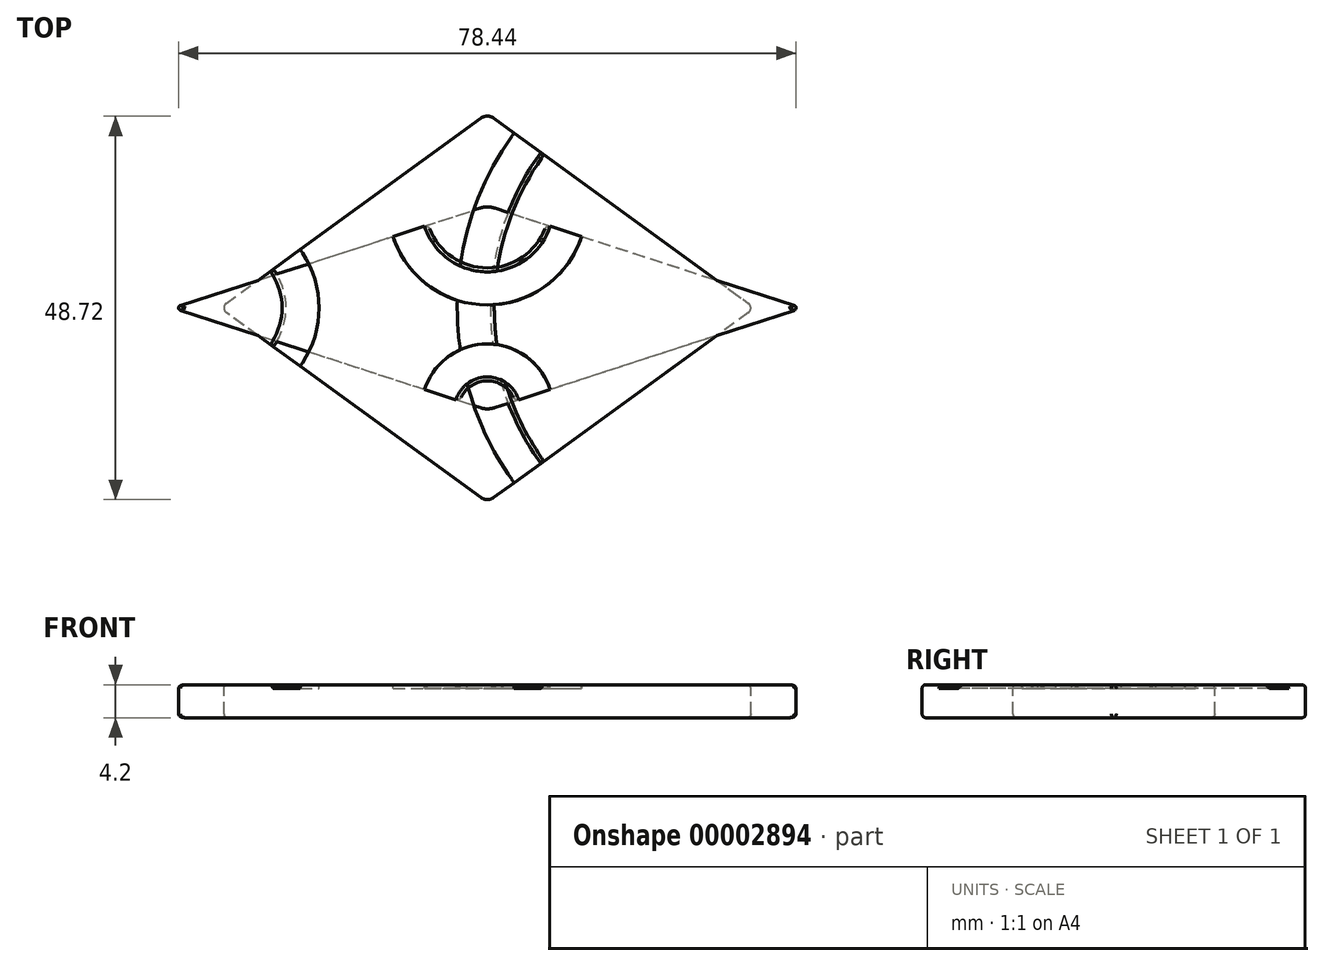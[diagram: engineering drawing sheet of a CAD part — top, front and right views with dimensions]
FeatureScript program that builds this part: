
annotation { "Feature Type Name" : "Feature", "Feature Type Description" : "" }
export const myFeature = defineFeature(function(context is Context, id is Id, definition is map)
    precondition{}
    {
        {
            var Q0;
            Q0=qCreatedBy(makeId("Top.planeOp"),FACE);
            var sketch = newSketch(context, id + "F0", { "sketchPlane" : qUnion([Q0])});
            skLineSegment(sketch, "E0", {"start": v(0.8, 24.1) * mm, "end": v(33.17, 0.59) * mm});
            skLineSegment(sketch, "E1", {"start": v(33.17, -0.59) * mm, "end": v(0.8, -24.1) * mm});
            skLineSegment(sketch, "E2", {"start": v(-0.8, -24.1) * mm, "end": v(-33.17, -0.59) * mm});
            skLineSegment(sketch, "E3", {"start": v(-33.17, 0.59) * mm, "end": v(-0.8, 24.1) * mm});
            skPoint(sketch, "E4.visualSharp", {"position": v(0, 24.69) * mm});
            skArc(sketch, "E4.filletArc", {"start": v(0.8, 24.1) * mm, "mid": v(0, 24.36) * mm, "end": v(-0.8, 24.1) * mm});
            skPoint(sketch, "E5.visualSharp", {"position": v(33.98, 0) * mm});
            skArc(sketch, "E5.filletArc", {"start": v(33.17, -0.59) * mm, "mid": v(33.47, 0) * mm, "end": v(33.17, 0.59) * mm});
            skPoint(sketch, "E6.visualSharp", {"position": v(0, -24.69) * mm});
            skArc(sketch, "E6.filletArc", {"start": v(-0.8, -24.1) * mm, "mid": v(0, -24.36) * mm, "end": v(0.8, -24.1) * mm});
            skPoint(sketch, "E7.visualSharp", {"position": v(-33.98, 0) * mm});
            skArc(sketch, "E7.filletArc", {"start": v(-33.17, 0.59) * mm, "mid": v(-33.47, 0) * mm, "end": v(-33.17, -0.59) * mm});
            skArc(sketch, "E8", {"start": v(6.8, 19.75) * mm, "mid": v(0.38, 0) * mm, "end": v(6.8, -19.75) * mm});
            skArc(sketch, "E9", {"start": v(3.4, 22.22) * mm, "mid": v(-3.82, 0) * mm, "end": v(3.4, -22.22) * mm});
            skArc(sketch, "E10", {"start": v(-27.18, -4.94) * mm, "mid": v(-25.58, 0) * mm, "end": v(-27.18, 4.94) * mm});
            skArc(sketch, "E11", {"start": v(-23.79, -7.4) * mm, "mid": v(-21.38, 0) * mm, "end": v(-23.79, 7.4) * mm});
            skSolve(sketch);
        }
        {
            var Q0;
            Q0 = qSketchRegion(id + "F0", true);
            extrude(context, id + "F1", {"entities" : qUnion([Q0]), "oppositeDirection" : true, "depth" : 4.2 * mm});
        }
        {
            var Q0;
            Q0=makeQuery(id+"F1.opExtrude","CAP_EDGE",EDGE,{"disambiguationData":[OSD([sQuery(id+"F0.wireOp",EDGE,"E2")])],"isStart":true});
            var Q1;
            Q1=makeQuery(id+"F1.opExtrude","CAP_EDGE",EDGE,{"disambiguationData":[OSD([sQuery(id+"F0.wireOp",EDGE,"E2")])],"isStart":false});
            fillet(context, id + "F2", {"entities" : qUnion([Q0, Q1]), "radius" : 0.5 * mm, "tangentPropagation" : true, "allowEdgeOverflow" : false});
        }
        {
            var Q0;
            {var subQ1=sQuery(id+"F0.wireOp",EDGE,"E8");Q0=makeQuery(id+"F0.imprint","IMPRINT",FACE,{"disambiguationData":[TD([[makeQuery(id+"F0.imprint","IMPRINT",EDGE,{"derivedFrom":subQ1}),-1.0]])]});}
            var Q1;
            {var subQ1=sQuery(id+"F0.wireOp",EDGE,"E10");Q1=makeQuery(id+"F0.imprint","IMPRINT",FACE,{"disambiguationData":[TD([[makeQuery(id+"F0.imprint","IMPRINT",EDGE,{"derivedFrom":subQ1}),-1.0]])]});}
            extrude(context, id + "F3", {"entities" : qUnion([Q0, Q1]), "operationType" : NewBodyOperationType.REMOVE, "oppositeDirection" : true, "depth" : 0.5 * mm});
        }
        {
            var Q0;
            Q0=makeQuery(id+"F3.boolean.opBoolean","COPY",EDGE,{"derivedFrom":makeQuery(id+"F3.opExtrude","CAP_EDGE",EDGE,{"disambiguationData":[OSD([sQuery(id+"F0.wireOp",EDGE,"E10")])],"isStart":true})});
            var Q1;
            Q1=makeQuery(id+"F3.boolean.opBoolean","COPY",EDGE,{"derivedFrom":makeQuery(id+"F3.opExtrude","CAP_EDGE",EDGE,{"disambiguationData":[OSD([sQuery(id+"F0.wireOp",EDGE,"E11")])],"isStart":true})});
            var Q2;
            Q2=makeQuery(id+"F3.boolean.opBoolean","COPY",EDGE,{"derivedFrom":makeQuery(id+"F3.opExtrude","CAP_EDGE",EDGE,{"disambiguationData":[OSD([sQuery(id+"F0.wireOp",EDGE,"E9")])],"isStart":true})});
            var Q3;
            Q3=makeQuery(id+"F3.boolean.opBoolean","COPY",EDGE,{"derivedFrom":makeQuery(id+"F3.opExtrude","CAP_EDGE",EDGE,{"disambiguationData":[OSD([sQuery(id+"F0.wireOp",EDGE,"E8")])],"isStart":true})});
            chamfer(context, id + "F4", {"entities" : qUnion([Q0, Q1, Q2, Q3]), "width" : 0.5 * mm, "tangentPropagation" : true});
        }
        {
            var Q0;
            Q0=qCreatedBy(makeId("Top.planeOp"),FACE);
            var sketch = newSketch(context, id + "F5", { "sketchPlane" : qUnion([Q0])});
            skLineSegment(sketch, "E12", {"start": v(-39, 0.3) * mm, "end": v(-0.95, 12.67) * mm});
            skLineSegment(sketch, "E13", {"start": v(0.95, 12.67) * mm, "end": v(39, 0.3) * mm});
            skLineSegment(sketch, "E14", {"start": v(39, -0.3) * mm, "end": v(0.95, -12.67) * mm});
            skLineSegment(sketch, "E15", {"start": v(-0.95, -12.67) * mm, "end": v(-39, -0.3) * mm});
            skPoint(sketch, "E16.visualSharp", {"position": v(0, 12.98) * mm});
            skArc(sketch, "E16.filletArc", {"start": v(0.95, 12.67) * mm, "mid": v(0, 12.82) * mm, "end": v(-0.95, 12.67) * mm});
            skPoint(sketch, "E17.visualSharp", {"position": v(39.94, 0) * mm});
            skArc(sketch, "E17.filletArc", {"start": v(39, -0.3) * mm, "mid": v(39.22, 0) * mm, "end": v(39, 0.3) * mm});
            skPoint(sketch, "E18.visualSharp", {"position": v(0, -12.98) * mm});
            skArc(sketch, "E18.filletArc", {"start": v(-0.95, -12.67) * mm, "mid": v(0, -12.82) * mm, "end": v(0.95, -12.67) * mm});
            skPoint(sketch, "E19.visualSharp", {"position": v(-39.94, 0) * mm});
            skArc(sketch, "E19.filletArc", {"start": v(-39, 0.3) * mm, "mid": v(-39.22, 0) * mm, "end": v(-39, -0.3) * mm});
            skArc(sketch, "E20", {"start": v(-7.99, 10.38) * mm, "mid": v(0, 4.58) * mm, "end": v(7.99, 10.38) * mm});
            skArc(sketch, "E21", {"start": v(-11.98, 9.09) * mm, "mid": v(0, 0.38) * mm, "end": v(11.98, 9.09) * mm});
            skArc(sketch, "E22", {"start": v(4, -11.68) * mm, "mid": v(0, -8.78) * mm, "end": v(-4, -11.68) * mm});
            skArc(sketch, "E23", {"start": v(7.99, -10.38) * mm, "mid": v(0, -4.58) * mm, "end": v(-7.99, -10.38) * mm});
            skSolve(sketch);
        }
        {
            var Q0;
            Q0 = qSketchRegion(id + "F5", true);
            extrude(context, id + "F6", {"entities" : qUnion([Q0]), "oppositeDirection" : true, "depth" : 4.2 * mm});
        }
        {
            var Q0;
            Q0=makeQuery(id+"F6.opExtrude","CAP_EDGE",EDGE,{"disambiguationData":[OSD([sQuery(id+"F5.wireOp",EDGE,"E15")])],"isStart":true});
            var Q1;
            Q1=makeQuery(id+"F6.opExtrude","CAP_EDGE",EDGE,{"disambiguationData":[OSD([sQuery(id+"F5.wireOp",EDGE,"E15")])],"isStart":false});
            fillet(context, id + "F7", {"entities" : qUnion([Q0, Q1]), "radius" : 0.5 * mm, "tangentPropagation" : true, "allowEdgeOverflow" : false});
        }
        {
            var Q0;
            {var subQ1=sQuery(id+"F5.wireOp",EDGE,"E20");Q0=makeQuery(id+"F5.imprint","IMPRINT",FACE,{"disambiguationData":[TD([[makeQuery(id+"F5.imprint","IMPRINT",EDGE,{"derivedFrom":subQ1}),-1.0]])]});}
            var Q1;
            {var subQ1=sQuery(id+"F5.wireOp",EDGE,"E22");Q1=makeQuery(id+"F5.imprint","IMPRINT",FACE,{"disambiguationData":[TD([[makeQuery(id+"F5.imprint","IMPRINT",EDGE,{"derivedFrom":subQ1}),-1.0]])]});}
            extrude(context, id + "F8", {"entities" : qUnion([Q0, Q1]), "operationType" : NewBodyOperationType.REMOVE, "oppositeDirection" : true, "depth" : 0.5 * mm});
        }
        {
            var Q0;
            Q0=makeQuery(id+"F8.boolean.opBoolean","COPY",EDGE,{"derivedFrom":makeQuery(id+"F8.opExtrude","CAP_EDGE",EDGE,{"disambiguationData":[OSD([sQuery(id+"F5.wireOp",EDGE,"E20")])],"isStart":true})});
            var Q1;
            Q1=makeQuery(id+"F8.boolean.opBoolean","COPY",EDGE,{"derivedFrom":makeQuery(id+"F8.opExtrude","CAP_EDGE",EDGE,{"disambiguationData":[OSD([sQuery(id+"F5.wireOp",EDGE,"E21")])],"isStart":true})});
            var Q2;
            Q2=makeQuery(id+"F8.boolean.opBoolean","COPY",EDGE,{"derivedFrom":makeQuery(id+"F8.opExtrude","CAP_EDGE",EDGE,{"disambiguationData":[OSD([sQuery(id+"F5.wireOp",EDGE,"E23")])],"isStart":true})});
            var Q3;
            Q3=makeQuery(id+"F8.boolean.opBoolean","COPY",EDGE,{"derivedFrom":makeQuery(id+"F8.opExtrude","CAP_EDGE",EDGE,{"disambiguationData":[OSD([sQuery(id+"F5.wireOp",EDGE,"E22")])],"isStart":true})});
            chamfer(context, id + "F9", {"entities" : qUnion([Q0, Q1, Q2, Q3]), "width" : 0.5 * mm, "tangentPropagation" : true});
        }
    });
